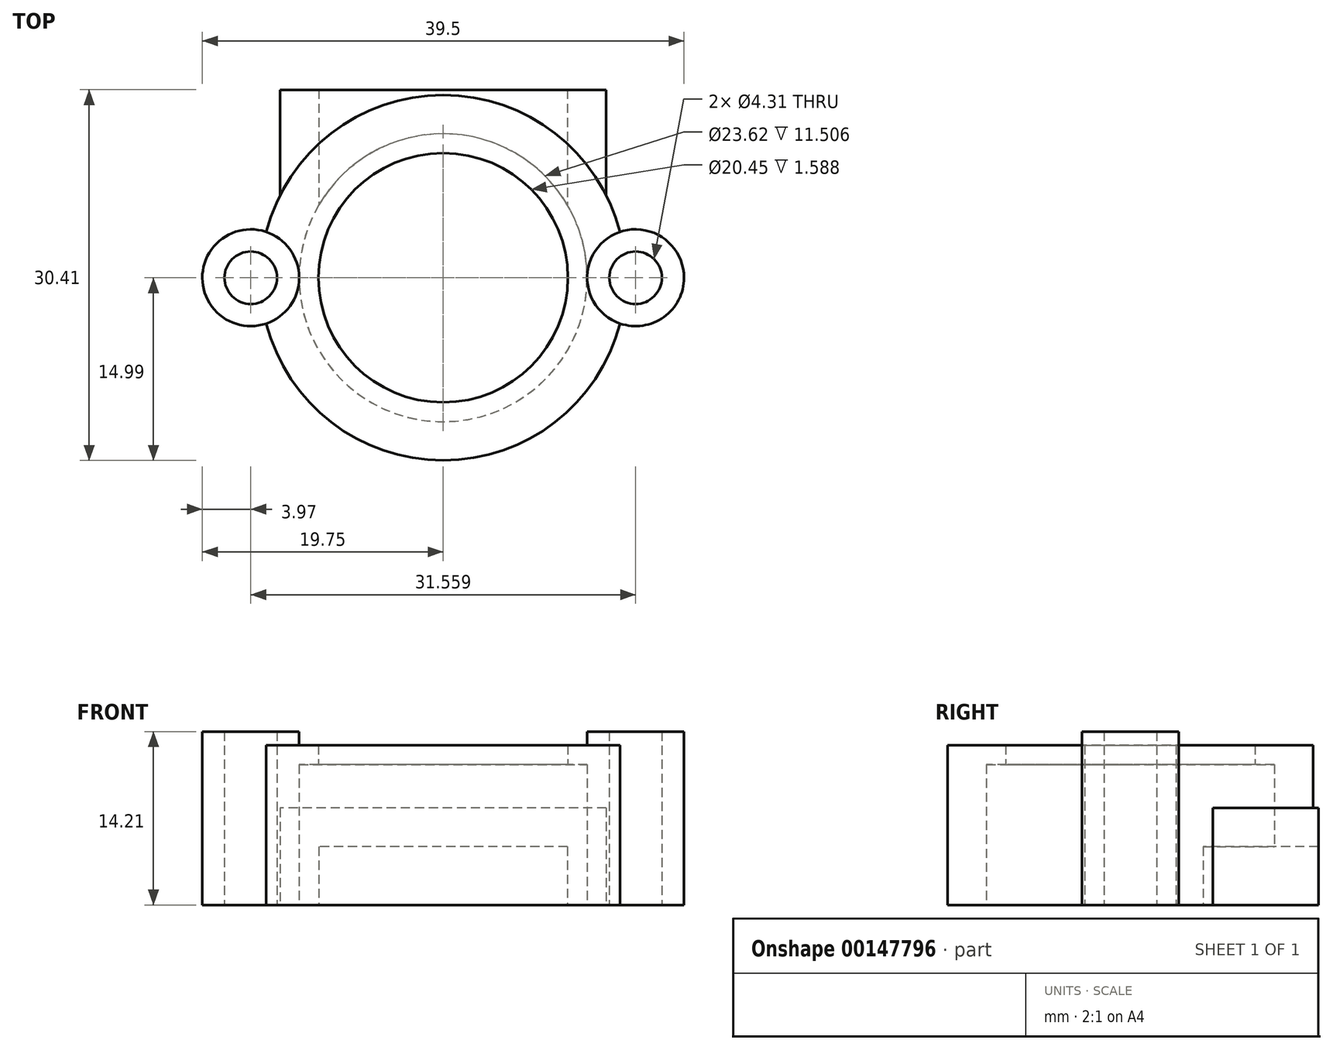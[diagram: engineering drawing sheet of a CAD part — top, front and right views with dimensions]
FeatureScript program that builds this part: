
annotation { "Feature Type Name" : "Feature", "Feature Type Description" : "" }
export const myFeature = defineFeature(function(context is Context, id is Id, definition is map)
    precondition{}
    {
        {
            var Q0;
            Q0=qCreatedBy(makeId("Top.planeOp"),FACE);
            var sketch = newSketch(context, id + "F0", { "sketchPlane" : qUnion([Q0])});
            skLineSegment(sketch, "E0", {"start": v(0, 0) * mm, "end": v(0, 15.42) * mm, "construction": true});
            skLineSegment(sketch, "E1.bottom", {"start": v(-10.2, 15.42) * mm, "end": v(10.2, 15.42) * mm, "construction": true});
            skLineSegment(sketch, "E1.left", {"start": v(-10.2, 15.42) * mm, "end": v(-10.2, 5.96) * mm});
            skLineSegment(sketch, "E1.right", {"start": v(10.2, 15.42) * mm, "end": v(10.2, 5.96) * mm});
            skArc(sketch, "E2", {"start": v(-10.2, 5.96) * mm, "mid": v(0, -11.81) * mm, "end": v(10.2, 5.96) * mm});
            skLineSegment(sketch, "E3", {"start": v(-15.78, 0) * mm, "end": v(15.78, 0) * mm, "construction": true});
            skCircle(sketch, "E4", {"center": v(-15.78, 0) * mm, "radius": 2.15 * mm});
            skCircle(sketch, "E5", {"center": v(15.78, 0) * mm, "radius": 2.15 * mm});
            skArc(sketch, "E6", {"start": v(-14.5, -3.76) * mm, "mid": v(0, -14.99) * mm, "end": v(14.5, -3.76) * mm});
            skLineSegment(sketch, "E7", {"start": v(-10.2, 15.42) * mm, "end": v(-13.37, 15.42) * mm});
            skLineSegment(sketch, "E8", {"start": v(-13.37, 15.42) * mm, "end": v(-13.37, 6.76) * mm});
            skLineSegment(sketch, "E9", {"start": v(10.2, 15.42) * mm, "end": v(13.37, 15.42) * mm});
            skLineSegment(sketch, "E10", {"start": v(13.37, 15.42) * mm, "end": v(13.37, 6.76) * mm});
            skArc(sketch, "E11", {"start": v(14.5, -3.76) * mm, "mid": v(19.75, 0) * mm, "end": v(14.5, 3.76) * mm});
            skArc(sketch, "E12", {"start": v(14.5, 3.76) * mm, "mid": v(14.02, 5.3) * mm, "end": v(13.37, 6.76) * mm});
            skArc(sketch, "E13", {"start": v(-14.5, 3.76) * mm, "mid": v(-19.75, 0) * mm, "end": v(-14.5, -3.76) * mm});
            skArc(sketch, "E14", {"start": v(-13.37, 6.76) * mm, "mid": v(-14.02, 5.3) * mm, "end": v(-14.5, 3.76) * mm});
            skSolve(sketch);
        }
        {
            var Q0;
            Q0=qSketchRegion(id+"F0",true);
            extrude(context, id + "F1", {"entities" : qUnion([Q0]), "depth" : 4.78 * mm});
        }
        {
            var Q0;
            Q0=makeQuery(id+"F1.opExtrude","CAP_FACE",FACE,{"disambiguationData":[OSD([sQuery(id+"F0.wireOp",EDGE,"E1.left"),sQuery(id+"F0.wireOp",EDGE,"E1.right"),sQuery(id+"F0.wireOp",EDGE,"E2"),sQuery(id+"F0.wireOp",EDGE,"E4"),sQuery(id+"F0.wireOp",EDGE,"E5"),sQuery(id+"F0.wireOp",EDGE,"E6"),sQuery(id+"F0.wireOp",EDGE,"E7"),sQuery(id+"F0.wireOp",EDGE,"E8"),sQuery(id+"F0.wireOp",EDGE,"E9"),sQuery(id+"F0.wireOp",EDGE,"E10"),sQuery(id+"F0.wireOp",EDGE,"E11"),sQuery(id+"F0.wireOp",EDGE,"E12"),sQuery(id+"F0.wireOp",EDGE,"E13"),sQuery(id+"F0.wireOp",EDGE,"E14")])],"isStart":false});
            var sketch = newSketch(context, id + "F2", { "sketchPlane" : qUnion([Q0])});
            skArc(sketch, "E15", {"start": v(-10.2, 5.96) * mm, "mid": v(0, -11.81) * mm, "end": v(10.2, 5.96) * mm});
            skArc(sketch, "E16", {"start": v(10.2, 5.96) * mm, "mid": v(0, 11.81) * mm, "end": v(-10.2, 5.96) * mm});
            skLineSegment(sketch, "E17.top", {"start": v(10.2, 15.42) * mm, "end": v(-10.2, 15.42) * mm});
            skLineSegment(sketch, "E17.left", {"start": v(10.2, 5.96) * mm, "end": v(10.2, 15.42) * mm});
            skLineSegment(sketch, "E17.right", {"start": v(-10.2, 5.96) * mm, "end": v(-10.2, 15.42) * mm});
            skLineSegment(sketch, "E18", {"start": v(10.2, 15.42) * mm, "end": v(13.37, 15.42) * mm});
            skLineSegment(sketch, "E19", {"start": v(13.37, 15.42) * mm, "end": v(13.37, 6.76) * mm});
            skLineSegment(sketch, "E20", {"start": v(-10.2, 15.42) * mm, "end": v(-13.37, 15.42) * mm});
            skLineSegment(sketch, "E21", {"start": v(-13.37, 15.42) * mm, "end": v(-13.37, 6.76) * mm});
            skArc(sketch, "E22", {"start": v(14.5, 3.76) * mm, "mid": v(14.02, 5.3) * mm, "end": v(13.37, 6.76) * mm});
            skArc(sketch, "E23", {"start": v(14.5, -3.76) * mm, "mid": v(19.75, 0) * mm, "end": v(14.5, 3.76) * mm});
            skArc(sketch, "E24", {"start": v(-14.5, 3.76) * mm, "mid": v(-19.75, 0) * mm, "end": v(-14.5, -3.76) * mm});
            skArc(sketch, "E25", {"start": v(-13.37, 6.76) * mm, "mid": v(-14.02, 5.3) * mm, "end": v(-14.5, 3.76) * mm});
            skArc(sketch, "E26", {"start": v(-14.5, -3.76) * mm, "mid": v(0, -14.99) * mm, "end": v(14.5, -3.76) * mm});
            skCircle(sketch, "E27", {"center": v(15.78, 0) * mm, "radius": 2.15 * mm});
            skCircle(sketch, "E28", {"center": v(-15.78, 0) * mm, "radius": 2.15 * mm});
            skSolve(sketch);
        }
        {
            var Q0;
            Q0=qSketchRegion(id+"F2",true);
            extrude(context, id + "F3", {"entities" : qUnion([Q0]), "operationType" : NewBodyOperationType.ADD, "depth" : 3.17 * mm});
        }
        {
            var Q0;
            Q0=makeQuery(id+"F3.opExtrude","CAP_FACE",FACE,{"disambiguationData":[OSD([sQuery(id+"F2.wireOp",EDGE,"E15"),sQuery(id+"F2.wireOp",EDGE,"E16"),sQuery(id+"F2.wireOp",EDGE,"E17.top"),sQuery(id+"F2.wireOp",EDGE,"E18"),sQuery(id+"F2.wireOp",EDGE,"E19"),sQuery(id+"F2.wireOp",EDGE,"E20"),sQuery(id+"F2.wireOp",EDGE,"E21"),sQuery(id+"F2.wireOp",EDGE,"E22"),sQuery(id+"F2.wireOp",EDGE,"E23"),sQuery(id+"F2.wireOp",EDGE,"E24"),sQuery(id+"F2.wireOp",EDGE,"E25"),sQuery(id+"F2.wireOp",EDGE,"E26"),sQuery(id+"F2.wireOp",EDGE,"E27"),sQuery(id+"F2.wireOp",EDGE,"E28")])],"isStart":false});
            var sketch = newSketch(context, id + "F4", { "sketchPlane" : qUnion([Q0])});
            skCircle(sketch, "E29", {"center": v(0, 0) * mm, "radius": 11.81 * mm});
            skArc(sketch, "E30", {"start": v(-14.5, -3.76) * mm, "mid": v(0, -14.99) * mm, "end": v(14.5, -3.76) * mm});
            skArc(sketch, "E31", {"start": v(14.5, 3.76) * mm, "mid": v(0, 14.99) * mm, "end": v(-14.5, 3.76) * mm});
            skArc(sketch, "E32", {"start": v(-14.5, 3.76) * mm, "mid": v(-19.75, 0) * mm, "end": v(-14.5, -3.76) * mm});
            skArc(sketch, "E33", {"start": v(14.5, -3.76) * mm, "mid": v(19.75, 0) * mm, "end": v(14.5, 3.76) * mm});
            skCircle(sketch, "E34", {"center": v(-15.78, 0) * mm, "radius": 2.15 * mm});
            skCircle(sketch, "E35", {"center": v(15.78, 0) * mm, "radius": 2.15 * mm});
            skSolve(sketch);
        }
        {
            var Q0;
            Q0=qSketchRegion(id+"F4",true);
            extrude(context, id + "F5", {"entities" : qUnion([Q0]), "operationType" : NewBodyOperationType.ADD, "depth" : 3.56 * mm});
        }
        {
            var Q0;
            Q0=makeQuery(id+"F5.opExtrude","CAP_FACE",FACE,{"disambiguationData":[OSD([sQuery(id+"F4.wireOp",EDGE,"E29"),sQuery(id+"F4.wireOp",EDGE,"E30"),sQuery(id+"F4.wireOp",EDGE,"E31"),sQuery(id+"F4.wireOp",EDGE,"E32"),sQuery(id+"F4.wireOp",EDGE,"E33"),sQuery(id+"F4.wireOp",EDGE,"E34"),sQuery(id+"F4.wireOp",EDGE,"E35")])],"isStart":false});
            var sketch = newSketch(context, id + "F6", { "sketchPlane" : qUnion([Q0])});
            skCircle(sketch, "E36", {"center": v(0, 0) * mm, "radius": 10.22 * mm});
            skSolve(sketch);
        }
        {
            var Q0;
            Q0=makeQuery(id+"F6.imprint","IMPRINT",FACE,{"disambiguationData":[TD([[makeQuery(id+"F6.imprint","IMPRINT",EDGE,{"derivedFrom":sQuery(id+"F6.wireOp",EDGE,"E36")}),-1.0]])]});
            var Q1;
            Q1=makeQuery(id+"F6.imprint","IMPRINT",FACE,{"disambiguationData":[TD([[makeQuery(id+"F6.imprint","IMPRINT",EDGE,{"derivedFrom":makeQuery(id+"F5.opExtrude","CAP_EDGE",EDGE,{"disambiguationData":[OSD([sQuery(id+"F4.wireOp",EDGE,"E29")])],"isStart":false})}),-1.0]])]});
            extrude(context, id + "F7", {"entities" : qUnion([Q0, Q1]), "operationType" : NewBodyOperationType.ADD, "depth" : 1.59 * mm});
        }
        {
            var Q0;
            Q0=makeQuery(id+"F7.opExtrude","CAP_FACE",FACE,{"disambiguationData":[OSD([sQuery(id+"F4.wireOp",EDGE,"E30"),sQuery(id+"F4.wireOp",EDGE,"E31"),sQuery(id+"F4.wireOp",EDGE,"E32"),sQuery(id+"F4.wireOp",EDGE,"E33"),sQuery(id+"F4.wireOp",EDGE,"E34"),sQuery(id+"F4.wireOp",EDGE,"E35"),sQuery(id+"F6.wireOp",EDGE,"E36")])],"isStart":false});
            var sketch = newSketch(context, id + "F8", { "sketchPlane" : qUnion([Q0])});
            skCircle(sketch, "E37", {"center": v(-15.78, 0) * mm, "radius": 2.15 * mm});
            skCircle(sketch, "E38", {"center": v(-15.78, 0) * mm, "radius": 3.97 * mm});
            skCircle(sketch, "E39", {"center": v(15.78, 0) * mm, "radius": 3.97 * mm});
            skCircle(sketch, "E40", {"center": v(15.78, 0) * mm, "radius": 2.15 * mm});
            skSolve(sketch);
        }
        {
            var Q0;
            Q0=qSketchRegion(id+"F8",true);
            extrude(context, id + "F9", {"entities" : qUnion([Q0]), "operationType" : NewBodyOperationType.ADD, "depth" : 1.12 * mm});
        }
    });
